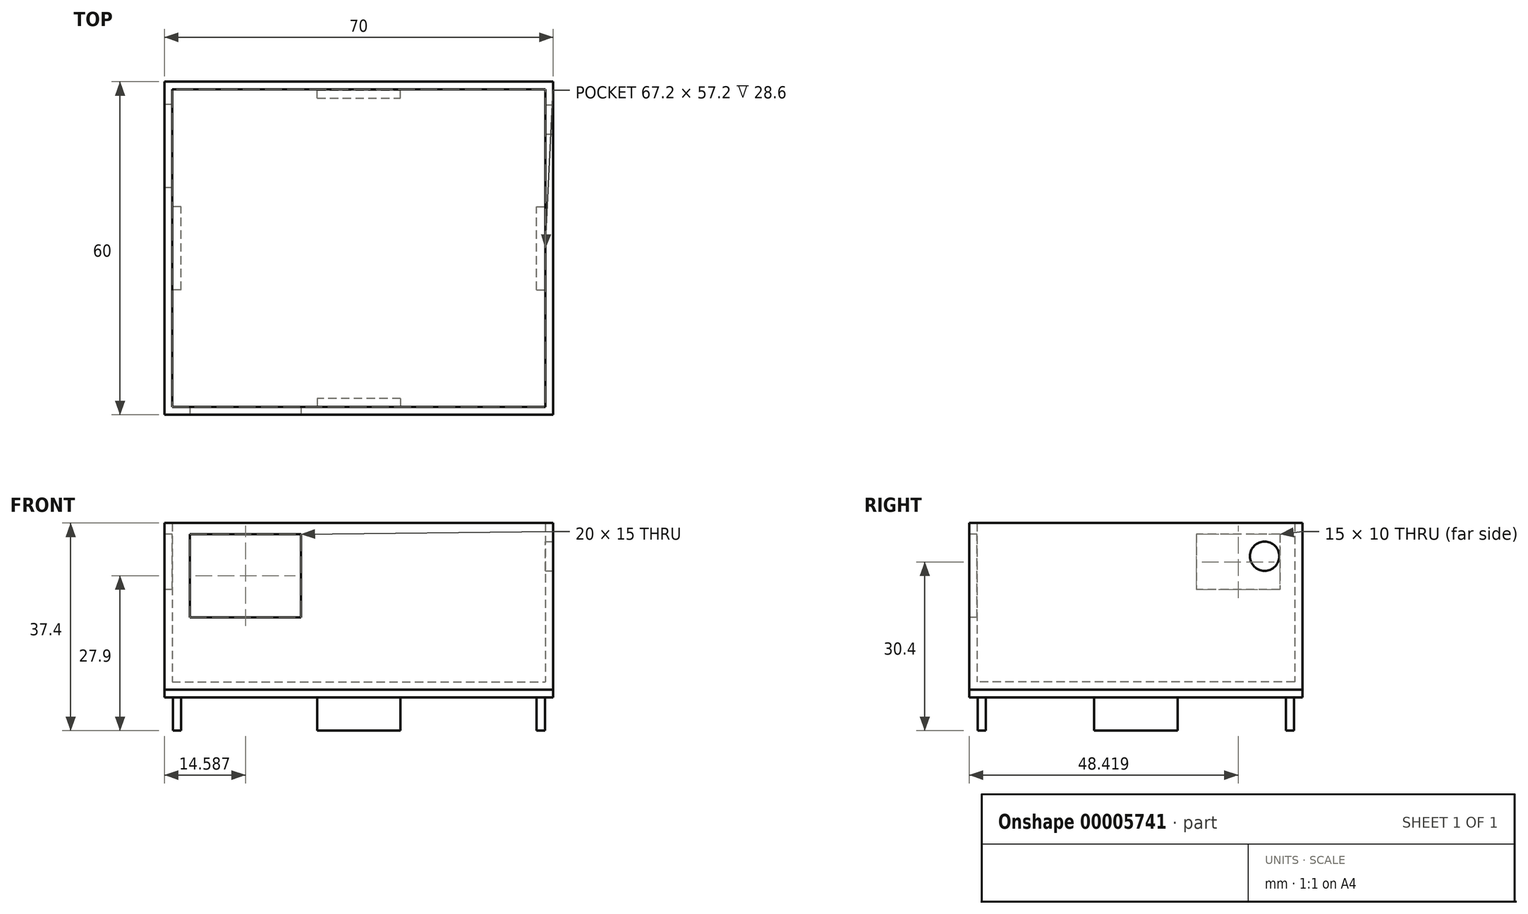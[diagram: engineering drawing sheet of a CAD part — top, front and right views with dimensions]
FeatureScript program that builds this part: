
annotation { "Feature Type Name" : "Feature", "Feature Type Description" : "" }
export const myFeature = defineFeature(function(context is Context, id is Id, definition is map)
    precondition{}
    {
        {
            var Q0;
            Q0=qCreatedBy(makeId("Top.planeOp"),FACE);
            var sketch = newSketch(context, id + "F0", { "sketchPlane" : qUnion([Q0])});
            skLineSegment(sketch, "E0.rect.bottom", {"start": v(-35, 30) * mm, "end": v(35, 30) * mm});
            skLineSegment(sketch, "E0.rect.top", {"start": v(-35, -30) * mm, "end": v(35, -30) * mm});
            skLineSegment(sketch, "E0.rect.left", {"start": v(-35, 30) * mm, "end": v(-35, -30) * mm});
            skLineSegment(sketch, "E0.rect.right", {"start": v(35, 30) * mm, "end": v(35, -30) * mm});
            skPoint(sketch, "E0.rect.middle", {"position": v(0, 0) * mm});
            skSolve(sketch);
        }
        {
            var Q0;
            Q0=makeQuery(id+"F0.imprint","IMPRINT",FACE,{"disambiguationData":[TD([[makeQuery(id+"F0.imprint","IMPRINT",EDGE,{"derivedFrom":sQuery(id+"F0.wireOp",EDGE,"E0.rect.bottom")}),-1.0]])]});
            extrude(context, id + "F1", {"entities" : qUnion([Q0]), "depth" : 30 * mm});
        }
        {
            var Q0;
            Q0=makeQuery(id+"F1.opExtrude","CAP_FACE",FACE,{"disambiguationData":[OSD([sQuery(id+"F0.wireOp",EDGE,"E0.rect.bottom"),sQuery(id+"F0.wireOp",EDGE,"E0.rect.top"),sQuery(id+"F0.wireOp",EDGE,"E0.rect.left"),sQuery(id+"F0.wireOp",EDGE,"E0.rect.right")])],"isStart":false});
            shell(context, id + "F2", {"entities" : qUnion([Q0]), "thickness" : 1.4 * mm});
        }
        {
            var Q0;
            Q0=makeQuery(id+"F1.opExtrude","SWEPT_FACE",FACE,{"disambiguationData":[OSD([sQuery(id+"F0.wireOp",EDGE,"E0.rect.top")])]});
            var sketch = newSketch(context, id + "F3", { "sketchPlane" : qUnion([Q0])});
            skLineSegment(sketch, "E1.bottom", {"start": v(-30.41, 28) * mm, "end": v(-10.41, 28) * mm});
            skLineSegment(sketch, "E1.top", {"start": v(-30.41, 13) * mm, "end": v(-10.41, 13) * mm});
            skLineSegment(sketch, "E1.left", {"start": v(-30.41, 28) * mm, "end": v(-30.41, 13) * mm});
            skLineSegment(sketch, "E1.right", {"start": v(-10.41, 28) * mm, "end": v(-10.41, 13) * mm});
            skSolve(sketch);
        }
        {
            var Q0;
            Q0=makeQuery(id+"F3.imprint","IMPRINT",FACE,{"disambiguationData":[TD([[makeQuery(id+"F3.imprint","IMPRINT",EDGE,{"derivedFrom":sQuery(id+"F3.wireOp",EDGE,"E1.bottom")}),-1.0]])]});
            extrude(context, id + "F4", {"entities" : qUnion([Q0]), "operationType" : NewBodyOperationType.REMOVE, "oppositeDirection" : true, "depth" : 25 * mm});
        }
        {
            var Q0;
            Q0=makeQuery(id+"F1.opExtrude","SWEPT_FACE",FACE,{"disambiguationData":[OSD([sQuery(id+"F0.wireOp",EDGE,"E0.rect.left")])]});
            var sketch = newSketch(context, id + "F5", { "sketchPlane" : qUnion([Q0])});
            skLineSegment(sketch, "E2.bottom", {"start": v(-25.92, 28) * mm, "end": v(-10.92, 28) * mm});
            skLineSegment(sketch, "E2.top", {"start": v(-25.92, 18) * mm, "end": v(-10.92, 18) * mm});
            skLineSegment(sketch, "E2.left", {"start": v(-25.92, 28) * mm, "end": v(-25.92, 18) * mm});
            skLineSegment(sketch, "E2.right", {"start": v(-10.92, 28) * mm, "end": v(-10.92, 18) * mm});
            skSolve(sketch);
        }
        {
            var Q0;
            Q0=makeQuery(id+"F5.imprint","IMPRINT",FACE,{"disambiguationData":[TD([[makeQuery(id+"F5.imprint","IMPRINT",EDGE,{"derivedFrom":sQuery(id+"F5.wireOp",EDGE,"E2.bottom")}),-1.0]])]});
            extrude(context, id + "F6", {"entities" : qUnion([Q0]), "operationType" : NewBodyOperationType.REMOVE, "oppositeDirection" : true, "depth" : 25 * mm});
        }
        {
            var Q0;
            Q0=makeQuery(id+"F1.opExtrude","SWEPT_FACE",FACE,{"disambiguationData":[OSD([sQuery(id+"F0.wireOp",EDGE,"E0.rect.right")])]});
            var sketch = newSketch(context, id + "F7", { "sketchPlane" : qUnion([Q0])});
            skCircle(sketch, "E3", {"center": v(23.19, 24.04) * mm, "radius": 2.64 * mm});
            skSolve(sketch);
        }
        {
            var Q0;
            Q0=makeQuery(id+"F7.imprint","IMPRINT",FACE,{"disambiguationData":[TD([[makeQuery(id+"F7.imprint","IMPRINT",EDGE,{"derivedFrom":sQuery(id+"F7.wireOp",EDGE,"E3")}),1.0]])]});
            extrude(context, id + "F8", {"entities" : qUnion([Q0]), "operationType" : NewBodyOperationType.REMOVE, "oppositeDirection" : true, "depth" : 25 * mm});
        }
        {
            var Q0;
            Q0=makeQuery(id+"F1.opExtrude","CAP_FACE",FACE,{"disambiguationData":[OSD([sQuery(id+"F0.wireOp",EDGE,"E0.rect.bottom"),sQuery(id+"F0.wireOp",EDGE,"E0.rect.top"),sQuery(id+"F0.wireOp",EDGE,"E0.rect.left"),sQuery(id+"F0.wireOp",EDGE,"E0.rect.right")])],"isStart":true});
            extrude(context, id + "F9", {"entities" : qUnion([Q0]), "depth" : 1.4 * mm});
        }
        {
            var Q0;
            Q0=makeQuery(id+"F9.opExtrude","CAP_FACE",FACE,{"disambiguationData":[OSD([sQuery(id+"F0.wireOp",EDGE,"E0.rect.bottom"),sQuery(id+"F0.wireOp",EDGE,"E0.rect.top"),sQuery(id+"F0.wireOp",EDGE,"E0.rect.left"),sQuery(id+"F0.wireOp",EDGE,"E0.rect.right")])],"isStart":false});
            var sketch = newSketch(context, id + "F10", { "sketchPlane" : qUnion([Q0])});
            skLineSegment(sketch, "E4.0", {"start": v(-33.5, -28.5) * mm, "end": v(33.5, -28.5) * mm});
            skLineSegment(sketch, "E4.1", {"start": v(-33.5, 28.5) * mm, "end": v(-33.5, -28.5) * mm});
            skLineSegment(sketch, "E4.2", {"start": v(33.5, 28.5) * mm, "end": v(-33.5, 28.5) * mm});
            skLineSegment(sketch, "E4.3", {"start": v(33.5, -28.5) * mm, "end": v(33.5, 28.5) * mm});
            skLineSegment(sketch, "E5.rect.bottom", {"start": v(7.5, 27.03) * mm, "end": v(-7.5, 27.03) * mm});
            skLineSegment(sketch, "E5.rect.top", {"start": v(7.5, 29.97) * mm, "end": v(-7.5, 29.97) * mm});
            skLineSegment(sketch, "E5.rect.left", {"start": v(7.5, 27.03) * mm, "end": v(7.5, 29.97) * mm});
            skLineSegment(sketch, "E5.rect.right", {"start": v(-7.5, 27.03) * mm, "end": v(-7.5, 29.97) * mm});
            skPoint(sketch, "E5.rect.middle", {"position": v(0, 28.5) * mm});
            skLineSegment(sketch, "E6.rect.bottom", {"start": v(-32.03, 7.5) * mm, "end": v(-34.97, 7.5) * mm});
            skLineSegment(sketch, "E6.rect.top", {"start": v(-32.03, -7.5) * mm, "end": v(-34.97, -7.5) * mm});
            skLineSegment(sketch, "E6.rect.left", {"start": v(-32.03, 7.5) * mm, "end": v(-32.03, -7.5) * mm});
            skLineSegment(sketch, "E6.rect.right", {"start": v(-34.97, 7.5) * mm, "end": v(-34.97, -7.5) * mm});
            skPoint(sketch, "E6.rect.middle", {"position": v(-33.5, 0) * mm});
            skLineSegment(sketch, "E7.rect.bottom", {"start": v(32.03, 7.5) * mm, "end": v(34.97, 7.5) * mm});
            skLineSegment(sketch, "E7.rect.top", {"start": v(32.03, -7.5) * mm, "end": v(34.97, -7.5) * mm});
            skLineSegment(sketch, "E7.rect.left", {"start": v(32.03, 7.5) * mm, "end": v(32.03, -7.5) * mm});
            skLineSegment(sketch, "E7.rect.right", {"start": v(34.97, 7.5) * mm, "end": v(34.97, -7.5) * mm});
            skPoint(sketch, "E7.rect.middle", {"position": v(33.5, 0) * mm});
            skLineSegment(sketch, "E8.rect.bottom", {"start": v(-7.5, -27.03) * mm, "end": v(7.5, -27.03) * mm});
            skLineSegment(sketch, "E8.rect.top", {"start": v(-7.5, -29.97) * mm, "end": v(7.5, -29.97) * mm});
            skLineSegment(sketch, "E8.rect.left", {"start": v(-7.5, -27.03) * mm, "end": v(-7.5, -29.97) * mm});
            skLineSegment(sketch, "E8.rect.right", {"start": v(7.5, -27.03) * mm, "end": v(7.5, -29.97) * mm});
            skPoint(sketch, "E8.rect.middle", {"position": v(0, -28.5) * mm});
            skSolve(sketch);
        }
        {
            var Q0;
            {var subQ0=sQuery(id+"F10.wireOp",EDGE,"E6.rect.left");Q0=makeQuery(id+"F10.imprint","IMPRINT",FACE,{"disambiguationData":[TD([[makeQuery(id+"F10.imprint","IMPRINT",EDGE,{"derivedFrom":subQ0}),-1.0]])]});}
            var Q1;
            {var subQ3=sQuery(id+"F10.wireOp",EDGE,"E5.rect.bottom");Q1=makeQuery(id+"F10.imprint","IMPRINT",FACE,{"disambiguationData":[TD([[makeQuery(id+"F10.imprint","IMPRINT",EDGE,{"derivedFrom":subQ3}),-1.0]])]});}
            var Q2;
            {var subQ0=sQuery(id+"F10.wireOp",EDGE,"E7.rect.left");Q2=makeQuery(id+"F10.imprint","IMPRINT",FACE,{"disambiguationData":[TD([[makeQuery(id+"F10.imprint","IMPRINT",EDGE,{"derivedFrom":subQ0}),1.0]])]});}
            var Q3;
            {var subQ3=sQuery(id+"F10.wireOp",EDGE,"E8.rect.bottom");Q3=makeQuery(id+"F10.imprint","IMPRINT",FACE,{"disambiguationData":[TD([[makeQuery(id+"F10.imprint","IMPRINT",EDGE,{"derivedFrom":subQ3}),-1.0]])]});}
            extrude(context, id + "F11", {"entities" : qUnion([Q0, Q1, Q2, Q3]), "operationType" : NewBodyOperationType.ADD, "depth" : 6 * mm});
        }
    });
